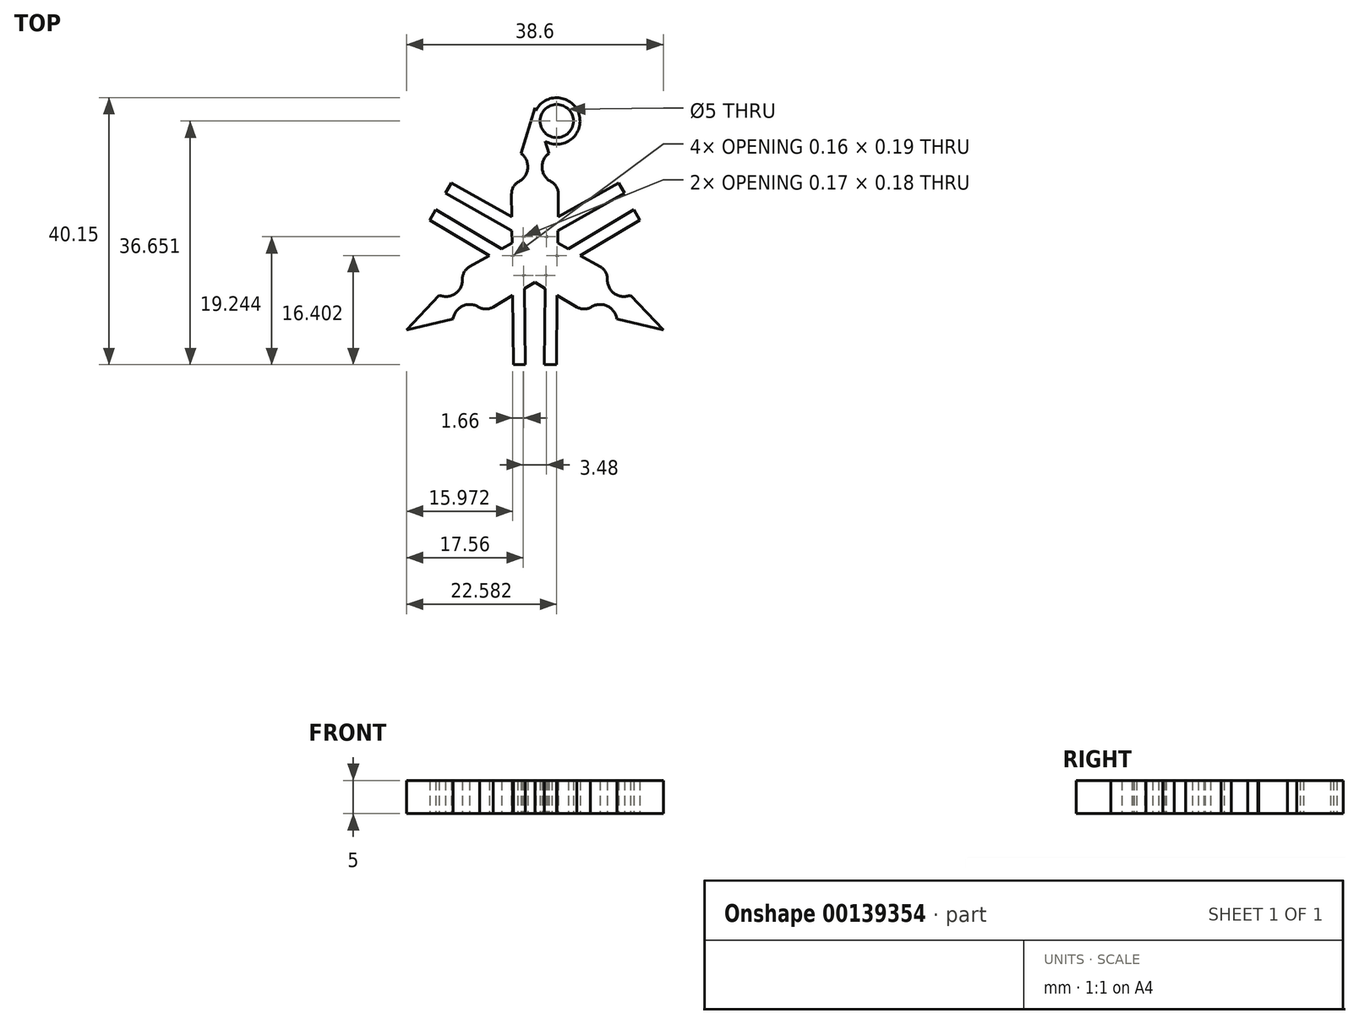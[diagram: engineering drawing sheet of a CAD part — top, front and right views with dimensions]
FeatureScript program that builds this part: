
annotation { "Feature Type Name" : "Feature", "Feature Type Description" : "" }
export const myFeature = defineFeature(function(context is Context, id is Id, definition is map)
    precondition{}
    {
        {
            var Q0;
            Q0=qCreatedBy(makeId("Top.planeOp"),FACE);
            var sketch = newSketch(context, id + "F0", { "sketchPlane" : qUnion([Q0])});
            skLineSegment(sketch, "E0", {"start": v(-1.43, -16.36) * mm, "end": v(-3.22, -16.36) * mm});
            skLineSegment(sketch, "E1", {"start": v(-2.08, 15.41) * mm, "end": v(0, 22.3) * mm});
            skArc(sketch, "E2", {"start": v(-2.57, 11.1) * mm, "mid": v(-1.09, 13.12) * mm, "end": v(-2.08, 15.41) * mm});
            skArc(sketch, "E3", {"start": v(-2.57, 11.1) * mm, "mid": v(-3.26, 10.31) * mm, "end": v(-3.51, 9.3) * mm});
            skArc(sketch, "E4", {"start": v(0.03, 10.45) * mm, "mid": v(-1.22, 9.91) * mm, "end": v(-1.73, 8.66) * mm});
            skPoint(sketch, "E5.orphan", {"position": v(0, 19.37) * mm});
            skPoint(sketch, "E6.MirrorCS.end.orphan", {"position": v(0.05, -23.26) * mm});
            skPoint(sketch, "E6.MirrorCS.start.orphan", {"position": v(0.05, 23.3) * mm});
            skPoint(sketch, "E7.MirrorCS.end.orphan", {"position": v(0.05, -24.07) * mm});
            skPoint(sketch, "E7.MirrorCS.start.orphan", {"position": v(0.05, 24.43) * mm});
            skPoint(sketch, "E8.MirrorCS.end.orphan", {"position": v(0.05, 22.3) * mm});
            skLineSegment(sketch, "E9", {"start": v(-3.51, 9.3) * mm, "end": v(-3.22, -16.36) * mm});
            skLineSegment(sketch, "E10.MirrorCS", {"start": v(2.08, 15.41) * mm, "end": v(1.52, 17.27) * mm});
            skArc(sketch, "E11.MirrorCS", {"start": v(2.57, 11.1) * mm, "mid": v(1.09, 13.12) * mm, "end": v(2.08, 15.41) * mm});
            skArc(sketch, "E12.MirrorCS", {"start": v(2.57, 11.1) * mm, "mid": v(3.26, 10.31) * mm, "end": v(3.51, 9.3) * mm});
            skArc(sketch, "E13.MirrorCS", {"start": v(-0.03, 10.45) * mm, "mid": v(1.22, 9.91) * mm, "end": v(1.73, 8.66) * mm});
            skLineSegment(sketch, "E14.MirrorCS", {"start": v(3.51, 9.3) * mm, "end": v(3.22, -16.36) * mm});
            skLineSegment(sketch, "E15.MirrorCS", {"start": v(1.43, -16.36) * mm, "end": v(3.22, -16.36) * mm});
            skLineSegment(sketch, "E16", {"start": v(-1.43, -16.36) * mm, "end": v(-1.73, 8.66) * mm});
            skLineSegment(sketch, "E17.MirrorCS", {"start": v(1.43, -16.36) * mm, "end": v(1.73, 8.66) * mm});
            skPoint(sketch, "E18.1.0", {"position": v(-20.2, -11.6) * mm});
            skLineSegment(sketch, "E18.1.1", {"start": v(-12.3, -9.5) * mm, "end": v(-19.3, -11.15) * mm});
            skArc(sketch, "E18.1.2", {"start": v(-9.06, -5.2) * mm, "mid": v(-7.98, -6) * mm, "end": v(-6.63, -5.83) * mm});
            skArc(sketch, "E18.1.3", {"start": v(-10.9, -3.32) * mm, "mid": v(-10.56, -2.33) * mm, "end": v(-9.8, -1.6) * mm});
            skLineSegment(sketch, "E18.1.4", {"start": v(-6.3, -7.7) * mm, "end": v(15.78, 5.39) * mm});
            skLineSegment(sketch, "E18.1.5", {"start": v(14.88, 6.94) * mm, "end": v(-6.63, -5.83) * mm});
            skLineSegment(sketch, "E18.1.6", {"start": v(13.45, 9.41) * mm, "end": v(12.55, 10.97) * mm});
            skArc(sketch, "E18.1.7", {"start": v(-8.33, -7.78) * mm, "mid": v(-7.3, -7.98) * mm, "end": v(-6.3, -7.7) * mm});
            skArc(sketch, "E18.1.8", {"start": v(-9.04, -5.25) * mm, "mid": v(-9.2, -3.9) * mm, "end": v(-8.36, -2.83) * mm});
            skPoint(sketch, "E18.1.9", {"position": v(-19.33, -11.1) * mm});
            skPoint(sketch, "E18.1.10", {"position": v(-21.18, -12.17) * mm});
            skArc(sketch, "E18.1.11", {"start": v(-8.33, -7.78) * mm, "mid": v(-10.81, -7.5) * mm, "end": v(-12.3, -9.5) * mm});
            skLineSegment(sketch, "E18.1.12", {"start": v(14.88, 6.94) * mm, "end": v(15.78, 5.39) * mm});
            skLineSegment(sketch, "E18.1.13", {"start": v(-14.39, -5.9) * mm, "end": v(-19.3, -11.15) * mm});
            skPoint(sketch, "E18.1.14", {"position": v(-16.78, -9.69) * mm});
            skLineSegment(sketch, "E18.1.15", {"start": v(-9.8, -1.6) * mm, "end": v(12.55, 10.97) * mm});
            skArc(sketch, "E18.1.16", {"start": v(-10.9, -3.32) * mm, "mid": v(-11.9, -5.62) * mm, "end": v(-14.39, -5.9) * mm});
            skLineSegment(sketch, "E18.1.17", {"start": v(13.45, 9.41) * mm, "end": v(-8.36, -2.83) * mm});
            skPoint(sketch, "E18.2.0", {"position": v(20.15, -11.69) * mm});
            skLineSegment(sketch, "E18.2.1", {"start": v(14.39, -5.9) * mm, "end": v(19.3, -11.15) * mm});
            skArc(sketch, "E18.2.2", {"start": v(9.04, -5.25) * mm, "mid": v(9.2, -3.9) * mm, "end": v(8.36, -2.83) * mm});
            skArc(sketch, "E18.2.3", {"start": v(8.33, -7.78) * mm, "mid": v(7.3, -7.98) * mm, "end": v(6.3, -7.7) * mm});
            skLineSegment(sketch, "E18.2.4", {"start": v(9.8, -1.6) * mm, "end": v(-12.55, 10.97) * mm});
            skLineSegment(sketch, "E18.2.5", {"start": v(-13.45, 9.41) * mm, "end": v(8.36, -2.83) * mm});
            skLineSegment(sketch, "E18.2.6", {"start": v(-14.88, 6.94) * mm, "end": v(-15.78, 5.39) * mm});
            skArc(sketch, "E18.2.7", {"start": v(10.9, -3.32) * mm, "mid": v(10.56, -2.33) * mm, "end": v(9.8, -1.6) * mm});
            skArc(sketch, "E18.2.8", {"start": v(9.06, -5.2) * mm, "mid": v(7.98, -6) * mm, "end": v(6.63, -5.83) * mm});
            skPoint(sketch, "E18.2.9", {"position": v(19.28, -11.19) * mm});
            skPoint(sketch, "E18.2.10", {"position": v(21.13, -12.26) * mm});
            skArc(sketch, "E18.2.11", {"start": v(10.9, -3.32) * mm, "mid": v(11.9, -5.62) * mm, "end": v(14.39, -5.9) * mm});
            skLineSegment(sketch, "E18.2.12", {"start": v(-13.45, 9.41) * mm, "end": v(-12.55, 10.97) * mm});
            skLineSegment(sketch, "E18.2.13", {"start": v(12.3, -9.5) * mm, "end": v(19.3, -11.15) * mm});
            skPoint(sketch, "E18.2.14", {"position": v(16.78, -9.69) * mm});
            skLineSegment(sketch, "E18.2.15", {"start": v(6.3, -7.7) * mm, "end": v(-15.78, 5.39) * mm});
            skArc(sketch, "E18.2.16", {"start": v(8.33, -7.78) * mm, "mid": v(10.81, -7.5) * mm, "end": v(12.3, -9.5) * mm});
            skLineSegment(sketch, "E18.2.17", {"start": v(-14.88, 6.94) * mm, "end": v(6.63, -5.83) * mm});
            skPoint(sketch, "E18.center", {"position": v(0, 0) * mm});
            skCircle(sketch, "E19", {"center": v(3.28, 20.3) * mm, "radius": 3.5 * mm});
            skCircle(sketch, "E20", {"center": v(3.28, 20.3) * mm, "radius": 2.5 * mm});
            skLineSegment(sketch, "E21.trimOffspring", {"start": v(0.14, 21.83) * mm, "end": v(0, 22.3) * mm});
            skLineSegment(sketch, "E22", {"start": v(3.28, 20.3) * mm, "end": v(3.28, 23.8) * mm});
            skSolve(sketch);
        }
        {
            var Q0;
            Q0 = qSketchRegion(id + "F0", true);
            var Q1;
            {var subQ19=sQuery(id+"F0.wireOp",EDGE,"E2");Q1=makeQuery(id+"F0.imprint","IMPRINT",FACE,{"disambiguationData":[TD([[makeQuery(id+"F0.imprint","IMPRINT",EDGE,{"derivedFrom":subQ19}),-1.0]])]});}
            var Q2;
            {var subQ5=sQuery(id+"F0.wireOp",EDGE,"E18.1.6");Q2=makeQuery(id+"F0.imprint","IMPRINT",FACE,{"disambiguationData":[TD([[makeQuery(id+"F0.imprint","IMPRINT",EDGE,{"derivedFrom":subQ5}),1.0]])]});}
            var Q3;
            {var subQ0=sQuery(id+"F0.wireOp",EDGE,"E18.1.12");Q3=makeQuery(id+"F0.imprint","IMPRINT",FACE,{"disambiguationData":[TD([[makeQuery(id+"F0.imprint","IMPRINT",EDGE,{"derivedFrom":subQ0}),-1.0]])]});}
            var Q4;
            {var subQ6=sQuery(id+"F0.wireOp",EDGE,"E18.2.3");Q4=makeQuery(id+"F0.imprint","IMPRINT",FACE,{"disambiguationData":[TD([[makeQuery(id+"F0.imprint","IMPRINT",EDGE,{"derivedFrom":subQ6}),-1.0]])]});}
            var Q5;
            {var subQ0=sQuery(id+"F0.wireOp",EDGE,"E15.MirrorCS");Q5=makeQuery(id+"F0.imprint","IMPRINT",FACE,{"disambiguationData":[TD([[makeQuery(id+"F0.imprint","IMPRINT",EDGE,{"derivedFrom":subQ0}),1.0]])]});}
            var Q6;
            {var subQ0=sQuery(id+"F0.wireOp",EDGE,"E0");Q6=makeQuery(id+"F0.imprint","IMPRINT",FACE,{"disambiguationData":[TD([[makeQuery(id+"F0.imprint","IMPRINT",EDGE,{"derivedFrom":subQ0}),-1.0]])]});}
            var Q7;
            {var subQ13=sQuery(id+"F0.wireOp",EDGE,"E18.1.3");Q7=makeQuery(id+"F0.imprint","IMPRINT",FACE,{"disambiguationData":[TD([[makeQuery(id+"F0.imprint","IMPRINT",EDGE,{"derivedFrom":subQ13}),-1.0]])]});}
            var Q8;
            {var subQ5=sQuery(id+"F0.wireOp",EDGE,"E18.2.6");Q8=makeQuery(id+"F0.imprint","IMPRINT",FACE,{"disambiguationData":[TD([[makeQuery(id+"F0.imprint","IMPRINT",EDGE,{"derivedFrom":subQ5}),1.0]])]});}
            var Q9;
            {var subQ5=sQuery(id+"F0.wireOp",EDGE,"E18.2.12");Q9=makeQuery(id+"F0.imprint","IMPRINT",FACE,{"disambiguationData":[TD([[makeQuery(id+"F0.imprint","IMPRINT",EDGE,{"derivedFrom":subQ5}),-1.0]])]});}
            var Q10;
            {var subQ0=sQuery(id+"F0.wireOp",EDGE,"E18.2.4");var subQ1=sQuery(id+"F0.wireOp",EDGE,"E9");var subQ2=makeQuery(id+"F0.imprint","INTERSECT",VERTEX,{"derivedFrom":[subQ1,subQ0]});Q10=makeQuery(id+"F0.imprint","IMPRINT",FACE,{"disambiguationData":[TD([[makeQuery(id+"F0.imprint","IMPRINT",EDGE,{"disambiguationData":[TD([[subQ2,-1.0]])],"derivedFrom":subQ1}),1.0]])]});}
            var Q11;
            {var subQ0=sQuery(id+"F0.wireOp",EDGE,"E18.1.15");var subQ1=sQuery(id+"F0.wireOp",EDGE,"E16");var subQ2=makeQuery(id+"F0.imprint","INTERSECT",VERTEX,{"derivedFrom":[subQ1,subQ0]});Q11=makeQuery(id+"F0.imprint","IMPRINT",FACE,{"disambiguationData":[TD([[makeQuery(id+"F0.imprint","IMPRINT",EDGE,{"disambiguationData":[TD([[subQ2,-1.0]])],"derivedFrom":subQ1}),-1.0]])]});}
            var Q12;
            {var subQ3=sQuery(id+"F0.wireOp",EDGE,"E18.2.5");var subQ8=sQuery(id+"F0.wireOp",EDGE,"E16");var subQ11=makeQuery(id+"F0.imprint","INTERSECT",VERTEX,{"derivedFrom":[subQ8,subQ3]});Q12=makeQuery(id+"F0.imprint","IMPRINT",FACE,{"disambiguationData":[TD([[makeQuery(id+"F0.imprint","IMPRINT",EDGE,{"disambiguationData":[TD([[subQ11,-1.0]])],"derivedFrom":subQ8}),-1.0]])]});}
            var Q13;
            {var subQ0=sQuery(id+"F0.wireOp",EDGE,"E18.2.4");var subQ1=sQuery(id+"F0.wireOp",EDGE,"E17.MirrorCS");var subQ2=makeQuery(id+"F0.imprint","INTERSECT",VERTEX,{"derivedFrom":[subQ1,subQ0]});Q13=makeQuery(id+"F0.imprint","IMPRINT",FACE,{"disambiguationData":[TD([[makeQuery(id+"F0.imprint","IMPRINT",EDGE,{"disambiguationData":[TD([[subQ2,-1.0]])],"derivedFrom":subQ1}),1.0]])]});}
            var Q14;
            {var subQ1=sQuery(id+"F0.wireOp",EDGE,"E14.MirrorCS");var subQ5=sQuery(id+"F0.wireOp",EDGE,"E18.1.15");var subQ6=makeQuery(id+"F0.imprint","INTERSECT",VERTEX,{"derivedFrom":[subQ1,subQ5]});Q14=makeQuery(id+"F0.imprint","IMPRINT",FACE,{"disambiguationData":[TD([[makeQuery(id+"F0.imprint","IMPRINT",EDGE,{"disambiguationData":[TD([[subQ6,-1.0]])],"derivedFrom":subQ1}),-1.0]])]});}
            var Q15;
            {var subQ5=sQuery(id+"F0.wireOp",EDGE,"E18.2.17");var subQ6=sQuery(id+"F0.wireOp",EDGE,"E9");var subQ7=makeQuery(id+"F0.imprint","INTERSECT",VERTEX,{"derivedFrom":[subQ6,subQ5]});Q15=makeQuery(id+"F0.imprint","IMPRINT",FACE,{"disambiguationData":[TD([[makeQuery(id+"F0.imprint","IMPRINT",EDGE,{"disambiguationData":[TD([[subQ7,-1.0]])],"derivedFrom":subQ6}),-1.0]])]});}
            var Q16;
            {var subQ0=sQuery(id+"F0.wireOp",EDGE,"E18.1.17");var subQ1=sQuery(id+"F0.wireOp",EDGE,"E9");var subQ2=makeQuery(id+"F0.imprint","INTERSECT",VERTEX,{"derivedFrom":[subQ1,subQ0]});Q16=makeQuery(id+"F0.imprint","IMPRINT",FACE,{"disambiguationData":[TD([[makeQuery(id+"F0.imprint","IMPRINT",EDGE,{"disambiguationData":[TD([[subQ2,-1.0]])],"derivedFrom":subQ1}),-1.0]])]});}
            var Q17;
            {var subQ0=sQuery(id+"F0.wireOp",EDGE,"E18.1.15");var subQ1=sQuery(id+"F0.wireOp",EDGE,"E9");var subQ2=makeQuery(id+"F0.imprint","INTERSECT",VERTEX,{"derivedFrom":[subQ1,subQ0]});Q17=makeQuery(id+"F0.imprint","IMPRINT",FACE,{"disambiguationData":[TD([[makeQuery(id+"F0.imprint","IMPRINT",EDGE,{"disambiguationData":[TD([[subQ2,-1.0]])],"derivedFrom":subQ1}),-1.0]])]});}
            var Q18;
            {var subQ0=sQuery(id+"F0.wireOp",EDGE,"E18.2.5");var subQ1=sQuery(id+"F0.wireOp",EDGE,"E9");var subQ2=makeQuery(id+"F0.imprint","INTERSECT",VERTEX,{"derivedFrom":[subQ1,subQ0]});Q18=makeQuery(id+"F0.imprint","IMPRINT",FACE,{"disambiguationData":[TD([[makeQuery(id+"F0.imprint","IMPRINT",EDGE,{"disambiguationData":[TD([[subQ2,-1.0]])],"derivedFrom":subQ1}),1.0]])]});}
            var Q19;
            {var subQ5=sQuery(id+"F0.wireOp",EDGE,"E18.1.15");var subQ6=sQuery(id+"F0.wireOp",EDGE,"E9");var subQ7=makeQuery(id+"F0.imprint","INTERSECT",VERTEX,{"derivedFrom":[subQ6,subQ5]});Q19=makeQuery(id+"F0.imprint","IMPRINT",FACE,{"disambiguationData":[TD([[makeQuery(id+"F0.imprint","IMPRINT",EDGE,{"disambiguationData":[TD([[subQ7,-1.0]])],"derivedFrom":subQ6}),1.0]])]});}
            var Q20;
            {var subQ0=sQuery(id+"F0.wireOp",EDGE,"E18.1.17");var subQ1=sQuery(id+"F0.wireOp",EDGE,"E9");var subQ2=makeQuery(id+"F0.imprint","INTERSECT",VERTEX,{"derivedFrom":[subQ1,subQ0]});Q20=makeQuery(id+"F0.imprint","IMPRINT",FACE,{"disambiguationData":[TD([[makeQuery(id+"F0.imprint","IMPRINT",EDGE,{"disambiguationData":[TD([[subQ2,-1.0]])],"derivedFrom":subQ1}),1.0]])]});}
            var Q21;
            {var subQ0=sQuery(id+"F0.wireOp",EDGE,"E18.1.5");var subQ1=sQuery(id+"F0.wireOp",EDGE,"E9");var subQ2=makeQuery(id+"F0.imprint","INTERSECT",VERTEX,{"derivedFrom":[subQ1,subQ0]});Q21=makeQuery(id+"F0.imprint","IMPRINT",FACE,{"disambiguationData":[TD([[makeQuery(id+"F0.imprint","IMPRINT",EDGE,{"disambiguationData":[TD([[subQ2,-1.0]])],"derivedFrom":subQ1}),1.0]])]});}
            var Q22;
            {var subQ0=sQuery(id+"F0.wireOp",EDGE,"E18.2.15");var subQ1=sQuery(id+"F0.wireOp",EDGE,"E9");var subQ2=makeQuery(id+"F0.imprint","INTERSECT",VERTEX,{"derivedFrom":[subQ1,subQ0]});Q22=makeQuery(id+"F0.imprint","IMPRINT",FACE,{"disambiguationData":[TD([[makeQuery(id+"F0.imprint","IMPRINT",EDGE,{"disambiguationData":[TD([[subQ2,-1.0]])],"derivedFrom":subQ1}),1.0]])]});}
            var Q23;
            {var subQ0=sQuery(id+"F0.wireOp",EDGE,"E18.1.17");var subQ1=sQuery(id+"F0.wireOp",EDGE,"E16");var subQ2=makeQuery(id+"F0.imprint","INTERSECT",VERTEX,{"derivedFrom":[subQ1,subQ0]});Q23=makeQuery(id+"F0.imprint","IMPRINT",FACE,{"disambiguationData":[TD([[makeQuery(id+"F0.imprint","IMPRINT",EDGE,{"disambiguationData":[TD([[subQ2,-1.0]])],"derivedFrom":subQ1}),-1.0]])]});}
            var Q24;
            {var subQ0=sQuery(id+"F0.wireOp",EDGE,"E18.2.17");var subQ1=sQuery(id+"F0.wireOp",EDGE,"E16");var subQ2=makeQuery(id+"F0.imprint","INTERSECT",VERTEX,{"derivedFrom":[subQ1,subQ0]});Q24=makeQuery(id+"F0.imprint","IMPRINT",FACE,{"disambiguationData":[TD([[makeQuery(id+"F0.imprint","IMPRINT",EDGE,{"disambiguationData":[TD([[subQ2,-1.0]])],"derivedFrom":subQ1}),1.0]])]});}
            var Q25;
            {var subQ0=sQuery(id+"F0.wireOp",EDGE,"E18.1.5");var subQ1=sQuery(id+"F0.wireOp",EDGE,"E17.MirrorCS");var subQ2=makeQuery(id+"F0.imprint","INTERSECT",VERTEX,{"derivedFrom":[subQ1,subQ0]});Q25=makeQuery(id+"F0.imprint","IMPRINT",FACE,{"disambiguationData":[TD([[makeQuery(id+"F0.imprint","IMPRINT",EDGE,{"disambiguationData":[TD([[subQ2,-1.0]])],"derivedFrom":subQ1}),-1.0]])]});}
            var Q26;
            {var subQ1=sQuery(id+"F0.wireOp",EDGE,"E14.MirrorCS");var subQ8=sQuery(id+"F0.wireOp",EDGE,"E18.2.4");var subQ10=makeQuery(id+"F0.imprint","INTERSECT",VERTEX,{"derivedFrom":[subQ1,subQ8]});Q26=makeQuery(id+"F0.imprint","IMPRINT",FACE,{"disambiguationData":[TD([[makeQuery(id+"F0.imprint","IMPRINT",EDGE,{"disambiguationData":[TD([[subQ10,-1.0]])],"derivedFrom":subQ1}),-1.0]])]});}
            var Q27;
            {var subQ0=sQuery(id+"F0.wireOp",EDGE,"E18.1.17");var subQ1=sQuery(id+"F0.wireOp",EDGE,"E14.MirrorCS");var subQ2=makeQuery(id+"F0.imprint","INTERSECT",VERTEX,{"derivedFrom":[subQ1,subQ0]});Q27=makeQuery(id+"F0.imprint","IMPRINT",FACE,{"disambiguationData":[TD([[makeQuery(id+"F0.imprint","IMPRINT",EDGE,{"disambiguationData":[TD([[subQ2,-1.0]])],"derivedFrom":subQ1}),-1.0]])]});}
            var Q28;
            {var subQ0=sQuery(id+"F0.wireOp",EDGE,"E18.2.5");var subQ1=sQuery(id+"F0.wireOp",EDGE,"E17.MirrorCS");var subQ2=makeQuery(id+"F0.imprint","INTERSECT",VERTEX,{"derivedFrom":[subQ1,subQ0]});Q28=makeQuery(id+"F0.imprint","IMPRINT",FACE,{"disambiguationData":[TD([[makeQuery(id+"F0.imprint","IMPRINT",EDGE,{"disambiguationData":[TD([[subQ2,-1.0]])],"derivedFrom":subQ1}),1.0]])]});}
            var Q29;
            {var subQ0=sQuery(id+"F0.wireOp",EDGE,"E18.2.4");var subQ1=sQuery(id+"F0.wireOp",EDGE,"E14.MirrorCS");var subQ2=makeQuery(id+"F0.imprint","INTERSECT",VERTEX,{"derivedFrom":[subQ1,subQ0]});Q29=makeQuery(id+"F0.imprint","IMPRINT",FACE,{"disambiguationData":[TD([[makeQuery(id+"F0.imprint","IMPRINT",EDGE,{"disambiguationData":[TD([[subQ2,-1.0]])],"derivedFrom":subQ1}),1.0]])]});}
            var Q30;
            {var subQ3=sQuery(id+"F0.wireOp",EDGE,"E18.1.5");var subQ5=sQuery(id+"F0.wireOp",EDGE,"E14.MirrorCS");var subQ6=makeQuery(id+"F0.imprint","INTERSECT",VERTEX,{"derivedFrom":[subQ5,subQ3]});Q30=makeQuery(id+"F0.imprint","IMPRINT",FACE,{"disambiguationData":[TD([[makeQuery(id+"F0.imprint","IMPRINT",EDGE,{"disambiguationData":[TD([[subQ6,-1.0]])],"derivedFrom":subQ5}),1.0]])]});}
            var Q31;
            {var subQ0=sQuery(id+"F0.wireOp",EDGE,"E18.2.5");var subQ1=sQuery(id+"F0.wireOp",EDGE,"E14.MirrorCS");var subQ2=makeQuery(id+"F0.imprint","INTERSECT",VERTEX,{"derivedFrom":[subQ1,subQ0]});Q31=makeQuery(id+"F0.imprint","IMPRINT",FACE,{"disambiguationData":[TD([[makeQuery(id+"F0.imprint","IMPRINT",EDGE,{"disambiguationData":[TD([[subQ2,-1.0]])],"derivedFrom":subQ1}),1.0]])]});}
            var Q32;
            {var subQ3=sQuery(id+"F0.wireOp",EDGE,"E18.2.5");var subQ6=sQuery(id+"F0.wireOp",EDGE,"E14.MirrorCS");var subQ11=makeQuery(id+"F0.imprint","INTERSECT",VERTEX,{"derivedFrom":[subQ6,subQ3]});Q32=makeQuery(id+"F0.imprint","IMPRINT",FACE,{"disambiguationData":[TD([[makeQuery(id+"F0.imprint","IMPRINT",EDGE,{"disambiguationData":[TD([[subQ11,-1.0]])],"derivedFrom":subQ6}),-1.0]])]});}
            var Q33;
            {var subQ0=sQuery(id+"F0.wireOp",EDGE,"E18.2.17");var subQ1=sQuery(id+"F0.wireOp",EDGE,"E17.MirrorCS");var subQ2=makeQuery(id+"F0.imprint","INTERSECT",VERTEX,{"derivedFrom":[subQ1,subQ0]});Q33=makeQuery(id+"F0.imprint","IMPRINT",FACE,{"disambiguationData":[TD([[makeQuery(id+"F0.imprint","IMPRINT",EDGE,{"disambiguationData":[TD([[subQ2,-1.0]])],"derivedFrom":subQ1}),1.0]])]});}
            var Q34;
            {var subQ0=sQuery(id+"F0.wireOp",EDGE,"E18.1.5");var subQ1=sQuery(id+"F0.wireOp",EDGE,"E16");var subQ2=makeQuery(id+"F0.imprint","INTERSECT",VERTEX,{"derivedFrom":[subQ1,subQ0]});Q34=makeQuery(id+"F0.imprint","IMPRINT",FACE,{"disambiguationData":[TD([[makeQuery(id+"F0.imprint","IMPRINT",EDGE,{"disambiguationData":[TD([[subQ2,-1.0]])],"derivedFrom":subQ1}),-1.0]])]});}
            var Q35;
            {var subQ1=sQuery(id+"F0.wireOp",EDGE,"E16");var subQ9=sQuery(id+"F0.wireOp",EDGE,"E18.2.15");var subQ11=makeQuery(id+"F0.imprint","INTERSECT",VERTEX,{"derivedFrom":[subQ1,subQ9]});Q35=makeQuery(id+"F0.imprint","IMPRINT",FACE,{"disambiguationData":[TD([[makeQuery(id+"F0.imprint","IMPRINT",EDGE,{"disambiguationData":[TD([[subQ11,-1.0]])],"derivedFrom":subQ1}),-1.0]])]});}
            var Q36;
            {var subQ0=sQuery(id+"F0.wireOp",EDGE,"E18.2.15");var subQ1=sQuery(id+"F0.wireOp",EDGE,"E17.MirrorCS");var subQ2=makeQuery(id+"F0.imprint","INTERSECT",VERTEX,{"derivedFrom":[subQ1,subQ0]});Q36=makeQuery(id+"F0.imprint","IMPRINT",FACE,{"disambiguationData":[TD([[makeQuery(id+"F0.imprint","IMPRINT",EDGE,{"disambiguationData":[TD([[subQ2,-1.0]])],"derivedFrom":subQ1}),1.0]])]});}
            var Q37;
            {var subQ0=sQuery(id+"F0.wireOp",EDGE,"E18.1.4");var subQ1=sQuery(id+"F0.wireOp",EDGE,"E16");var subQ2=makeQuery(id+"F0.imprint","INTERSECT",VERTEX,{"derivedFrom":[subQ1,subQ0]});Q37=makeQuery(id+"F0.imprint","IMPRINT",FACE,{"disambiguationData":[TD([[makeQuery(id+"F0.imprint","IMPRINT",EDGE,{"disambiguationData":[TD([[subQ2,-1.0]])],"derivedFrom":subQ1}),-1.0]])]});}
            var Q38;
            {var subQ1=sQuery(id+"F0.wireOp",EDGE,"E14.MirrorCS");var subQ7=sQuery(id+"F0.wireOp",EDGE,"E18.2.17");var subQ9=makeQuery(id+"F0.imprint","INTERSECT",VERTEX,{"derivedFrom":[subQ1,subQ7]});Q38=makeQuery(id+"F0.imprint","IMPRINT",FACE,{"disambiguationData":[TD([[makeQuery(id+"F0.imprint","IMPRINT",EDGE,{"disambiguationData":[TD([[subQ9,-1.0]])],"derivedFrom":subQ1}),-1.0]])]});}
            var Q39;
            {var subQ0=sQuery(id+"F0.wireOp",EDGE,"E18.1.4");var subQ1=sQuery(id+"F0.wireOp",EDGE,"E14.MirrorCS");var subQ2=makeQuery(id+"F0.imprint","INTERSECT",VERTEX,{"derivedFrom":[subQ1,subQ0]});Q39=makeQuery(id+"F0.imprint","IMPRINT",FACE,{"disambiguationData":[TD([[makeQuery(id+"F0.imprint","IMPRINT",EDGE,{"disambiguationData":[TD([[subQ2,-1.0]])],"derivedFrom":subQ1}),-1.0]])]});}
            var Q40;
            {var subQ5=sQuery(id+"F0.wireOp",EDGE,"E16");var subQ6=sQuery(id+"F0.wireOp",EDGE,"E4");var subQ7=makeQuery(id+"F0.imprint","INTERSECT",VERTEX,{"derivedFrom":[subQ6,subQ5]});Q40=makeQuery(id+"F0.imprint","IMPRINT",FACE,{"disambiguationData":[TD([[makeQuery(id+"F0.imprint","IMPRINT",EDGE,{"disambiguationData":[TD([[subQ7,1.0]])],"derivedFrom":subQ6}),1.0]])]});}
            var Q41;
            {var subQ1=sQuery(id+"F0.wireOp",EDGE,"E16");var subQ9=sQuery(id+"F0.wireOp",EDGE,"E18.2.17");var subQ11=makeQuery(id+"F0.imprint","INTERSECT",VERTEX,{"derivedFrom":[subQ1,subQ9]});Q41=makeQuery(id+"F0.imprint","IMPRINT",FACE,{"disambiguationData":[TD([[makeQuery(id+"F0.imprint","IMPRINT",EDGE,{"disambiguationData":[TD([[subQ11,-1.0]])],"derivedFrom":subQ1}),-1.0]])]});}
            var Q42;
            {var subQ3=sQuery(id+"F0.wireOp",EDGE,"E9");var subQ5=sQuery(id+"F0.wireOp",EDGE,"E18.2.15");var subQ6=makeQuery(id+"F0.imprint","INTERSECT",VERTEX,{"derivedFrom":[subQ3,subQ5]});Q42=makeQuery(id+"F0.imprint","IMPRINT",FACE,{"disambiguationData":[TD([[makeQuery(id+"F0.imprint","IMPRINT",EDGE,{"disambiguationData":[TD([[subQ6,-1.0]])],"derivedFrom":subQ3}),-1.0]])]});}
            var Q43;
            {var subQ3=sQuery(id+"F0.wireOp",EDGE,"E18.1.4");var subQ7=sQuery(id+"F0.wireOp",EDGE,"E14.MirrorCS");var subQ8=makeQuery(id+"F0.imprint","INTERSECT",VERTEX,{"derivedFrom":[subQ7,subQ3]});Q43=makeQuery(id+"F0.imprint","IMPRINT",FACE,{"disambiguationData":[TD([[makeQuery(id+"F0.imprint","IMPRINT",EDGE,{"disambiguationData":[TD([[subQ8,-1.0]])],"derivedFrom":subQ7}),1.0]])]});}
            extrude(context, id + "F1", {"entities" : qUnion([Q0, Q1, Q2, Q3, Q4, Q5, Q6, Q7, Q8, Q9, Q10, Q11, Q12, Q13, Q14, Q15, Q16, Q17, Q18, Q19, Q20, Q21, Q22, Q23, Q24, Q25, Q26, Q27, Q28, Q29, Q30, Q31, Q32, Q33, Q34, Q35, Q36, Q37, Q38, Q39, Q40, Q41, Q42, Q43]), "depth" : 5 * mm});
        }
    });
